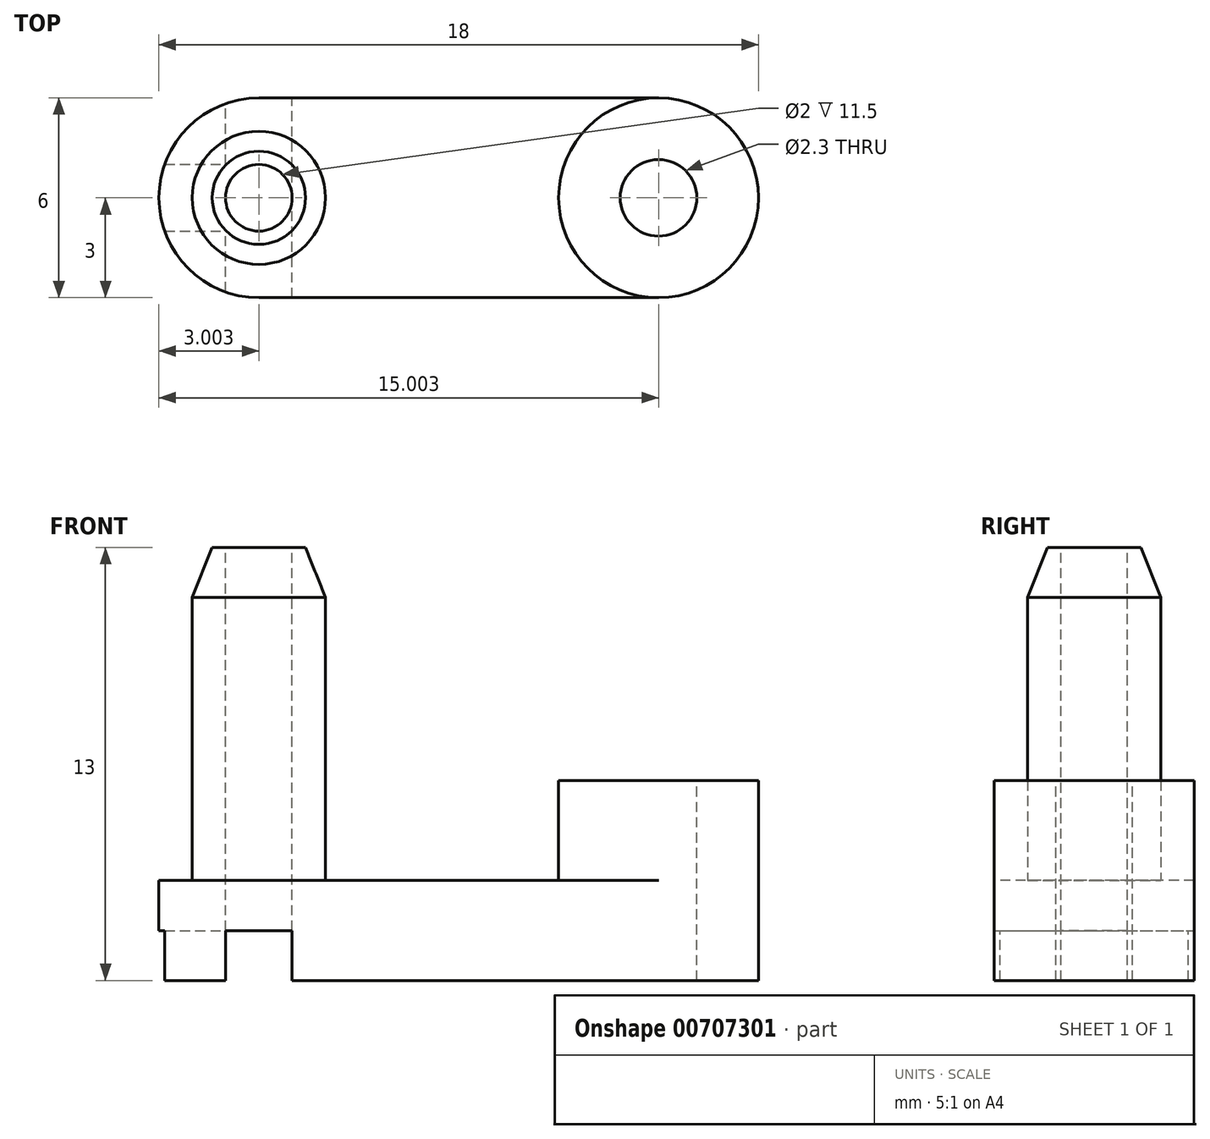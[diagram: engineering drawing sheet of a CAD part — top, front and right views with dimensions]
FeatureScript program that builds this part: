
annotation { "Feature Type Name" : "Feature", "Feature Type Description" : "" }
export const myFeature = defineFeature(function(context is Context, id is Id, definition is map)
    precondition{}
    {
        {
            var Q0;
            Q0=qCreatedBy(makeId("Top.planeOp"),FACE);
            var sketch = newSketch(context, id + "F0", { "sketchPlane" : qUnion([Q0])});
            skLineSegment(sketch, "E0.bottom", {"start": v(-7.1, 3) * mm, "end": v(10.9, 3) * mm});
            skLineSegment(sketch, "E0.top", {"start": v(-7.1, -3) * mm, "end": v(10.9, -3) * mm});
            skLineSegment(sketch, "E0.left", {"start": v(-7.1, 3) * mm, "end": v(-7.1, -3) * mm});
            skLineSegment(sketch, "E0.right", {"start": v(10.9, 3) * mm, "end": v(10.9, -3) * mm});
            skSolve(sketch);
        }
        {
            var Q0;
            Q0=qSketchRegion(id+"F0",true);
            extrude(context, id + "F1", {"entities" : qUnion([Q0]), "depth" : 3 * mm, "offsetDistance" : 25 * mm});
        }
        {
            var Q0;
            Q0=makeQuery(id+"F1.opExtrude","CAP_FACE",FACE,{"disambiguationData":[OSD([sQuery(id+"F0.wireOp",EDGE,"E0.bottom"),sQuery(id+"F0.wireOp",EDGE,"E0.top"),sQuery(id+"F0.wireOp",EDGE,"E0.left"),sQuery(id+"F0.wireOp",EDGE,"E0.right")])],"isStart":false});
            var sketch = newSketch(context, id + "F2", { "sketchPlane" : qUnion([Q0])});
            skCircle(sketch, "E1", {"center": v(7.9, 0) * mm, "radius": 3 * mm});
            skCircle(sketch, "E2", {"center": v(-4.1, 0) * mm, "radius": 2 * mm});
            skSolve(sketch);
        }
        {
            var Q0;
            Q0=qSketchRegion(id+"F2",true);
            extrude(context, id + "F3", {"entities" : qUnion([Q0]), "operationType" : NewBodyOperationType.ADD, "depth" : 10 * mm, "offsetDistance" : 25 * mm});
        }
        {
            var Q0;
            Q0=makeQuery(id+"F3.opExtrude","CAP_FACE",FACE,{"disambiguationData":[OSD([sQuery(id+"F2.wireOp",EDGE,"E2")])],"isStart":false});
            var sketch = newSketch(context, id + "F4", { "sketchPlane" : qUnion([Q0])});
            skCircle(sketch, "E3", {"center": v(-4.1, 0) * mm, "radius": 1 * mm});
            skCircle(sketch, "E4", {"center": v(7.9, 0) * mm, "radius": 1.15 * mm});
            skSolve(sketch);
        }
        {
            var Q0;
            Q0=qSketchRegion(id+"F4",true);
            extrude(context, id + "F5", {"entities" : qUnion([Q0]), "operationType" : NewBodyOperationType.REMOVE, "oppositeDirection" : true, "depth" : 20 * mm, "offsetDistance" : 25 * mm});
        }
        {
            var Q0;
            Q0=makeQuery(id+"F3.opExtrude","CAP_EDGE",EDGE,{"disambiguationData":[OSD([sQuery(id+"F2.wireOp",EDGE,"E2")])],"isStart":false});
            chamfer(context, id + "F6", {"entities" : qUnion([Q0]), "chamferType" : ChamferType.TWO_OFFSETS, "width1" : 0.6 * mm, "oppositeDirection" : false, "width2" : 1.5 * mm, "tangentPropagation" : true});
        }
        {
            var Q0;
            Q0=makeQuery(id+"F3.opExtrude","CAP_FACE",FACE,{"disambiguationData":[OSD([sQuery(id+"F2.wireOp",EDGE,"E1")])],"isStart":false});
            var sketch = newSketch(context, id + "F7", { "sketchPlane" : qUnion([Q0])});
            skLineSegment(sketch, "E5.bottom", {"start": v(1.79, 5.38) * mm, "end": v(13.39, 5.38) * mm});
            skLineSegment(sketch, "E5.top", {"start": v(1.79, -6.45) * mm, "end": v(13.39, -6.45) * mm});
            skLineSegment(sketch, "E5.left", {"start": v(1.79, 5.38) * mm, "end": v(1.79, -6.45) * mm});
            skLineSegment(sketch, "E5.right", {"start": v(13.39, 5.38) * mm, "end": v(13.39, -6.45) * mm});
            skSolve(sketch);
        }
        {
            var Q0;
            Q0=qSketchRegion(id+"F7",true);
            extrude(context, id + "F8", {"entities" : qUnion([Q0]), "operationType" : NewBodyOperationType.REMOVE, "oppositeDirection" : true, "depth" : 7 * mm, "offsetDistance" : 25 * mm});
        }
        {
            var Q0;
            Q0=makeQuery(id+"F1.opExtrude","SWEPT_EDGE",EDGE,{"disambiguationData":[OSD([sQuery(id+"F0.wireOp",EDGE,"E0.top"),sQuery(id+"F0.wireOp",EDGE,"E0.right")])]});
            var Q1;
            Q1=makeQuery(id+"F1.opExtrude","SWEPT_EDGE",EDGE,{"disambiguationData":[OSD([sQuery(id+"F0.wireOp",EDGE,"E0.bottom"),sQuery(id+"F0.wireOp",EDGE,"E0.right")])]});
            var Q2;
            Q2=makeQuery(id+"F1.opExtrude","SWEPT_EDGE",EDGE,{"disambiguationData":[OSD([sQuery(id+"F0.wireOp",EDGE,"E0.bottom"),sQuery(id+"F0.wireOp",EDGE,"E0.left")])]});
            var Q3;
            Q3=makeQuery(id+"F1.opExtrude","SWEPT_EDGE",EDGE,{"disambiguationData":[OSD([sQuery(id+"F0.wireOp",EDGE,"E0.top"),sQuery(id+"F0.wireOp",EDGE,"E0.left")])]});
            fillet(context, id + "F9", {"entities" : qUnion([Q0, Q1, Q2, Q3]), "radius" : 3 * mm, "tangentPropagation" : true, "allowEdgeOverflow" : false});
        }
        {
            var Q0;
            Q0=makeQuery(id+"F1.opExtrude","CAP_FACE",FACE,{"disambiguationData":[OSD([sQuery(id+"F0.wireOp",EDGE,"E0.bottom"),sQuery(id+"F0.wireOp",EDGE,"E0.top"),sQuery(id+"F0.wireOp",EDGE,"E0.left"),sQuery(id+"F0.wireOp",EDGE,"E0.right")])],"isStart":true});
            var sketch = newSketch(context, id + "F10", { "sketchPlane" : qUnion([Q0])});
            skLineSegment(sketch, "E6.bottom", {"start": v(-5.1, 5.62) * mm, "end": v(-3.1, 5.62) * mm});
            skLineSegment(sketch, "E6.top", {"start": v(-5.1, -5.57) * mm, "end": v(-3.1, -5.57) * mm});
            skLineSegment(sketch, "E6.left", {"start": v(-5.1, 5.62) * mm, "end": v(-5.1, -5.57) * mm});
            skLineSegment(sketch, "E6.right", {"start": v(-3.1, 5.62) * mm, "end": v(-3.1, -5.57) * mm});
            skLineSegment(sketch, "E7.bottom", {"start": v(-10.55, 1) * mm, "end": v(-5.1, 1) * mm});
            skLineSegment(sketch, "E7.top", {"start": v(-10.55, -1) * mm, "end": v(-5.1, -1) * mm});
            skLineSegment(sketch, "E7.left", {"start": v(-10.55, 1) * mm, "end": v(-10.55, -1) * mm});
            skLineSegment(sketch, "E7.right", {"start": v(-5.1, 1) * mm, "end": v(-5.1, -1) * mm});
            skSolve(sketch);
        }
        {
            var Q0;
            Q0 = qSketchRegion(id + "F10", true);
            extrude(context, id + "F11", {"entities" : qUnion([Q0]), "operationType" : NewBodyOperationType.REMOVE, "oppositeDirection" : true, "depth" : 1.5 * mm, "offsetDistance" : 25 * mm});
        }
    });
